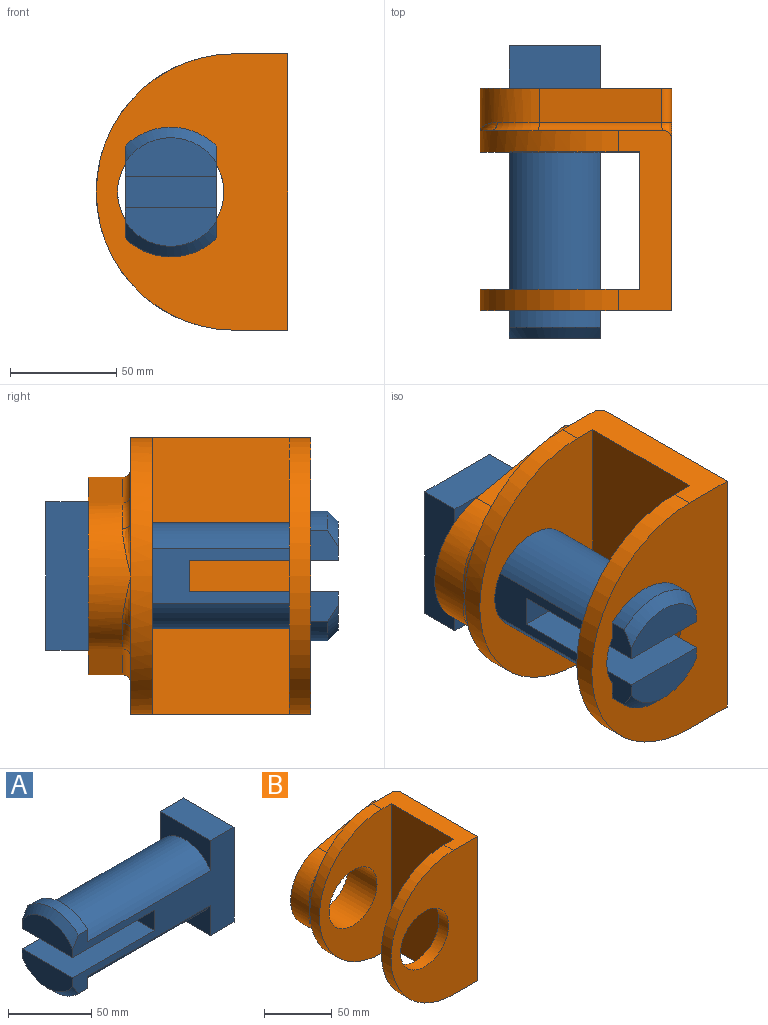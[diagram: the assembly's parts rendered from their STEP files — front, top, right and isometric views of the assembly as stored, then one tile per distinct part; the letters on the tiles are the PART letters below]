
ASSEMBLY  parts=2 mates=1
PART A: 20 faces, bbox 137.5x51.4x70 mm
  f0: plane 43x18mm, normal (-1,0,0), area 624.6mm2, adj f1,f7,f11,f19
  f1: plane 137.5x70mm, normal (0,-1,0), area 3540.9mm2, adj f0,f2,f3,f4,f5,f6,f8,f9
  f2: plane 43x22.24mm, normal (-1,0,0), area 583.7mm2, adj f1,f4,f7,f16
  f3: plane 70x43mm, normal (1,0,0), area 3010mm2, adj f1,f4,f6,f7
  f4: plane 43x20mm, normal (0,0,1), area 860mm2, adj f1,f2,f3,f7
  f5: plane 43x22.24mm, normal (-1,0,0), area 583.7mm2, adj f1,f6,f7,f15
  f6: plane 43x20mm, normal (0,0,-1), area 860mm2, adj f1,f3,f5,f7
  f7: plane 137.5x70mm, normal (0,1,0), area 3540.9mm2, adj f0,f2,f3,f4,f5,f6,f8,f9
  f8: cylinder r=30.5mm len=43mm, axis (1,0,0), area 381.8mm2, adj f1,f7,f14,f18
  f9: cylinder r=30.5mm len=43mm, axis (1,0,0), area 381.8mm2, adj f1,f7,f17,f19
  f10: plane 43x18mm, normal (-1,0,0), area 624.6mm2, adj f1,f7,f12,f18
  f11: plane 70x43mm, normal (0,0,-1), area 3010mm2, adj f0,f1,f7,f13
  f12: plane 70x43mm, normal (0,0,1), area 3010mm2, adj f1,f7,f10,f13
  f13: plane 43x15mm, normal (-1,0,0), area 645mm2, adj f1,f7,f11,f12
  f14: plane 43x17.74mm, normal (1,0,0), area 271.5mm2, adj f1,f7,f8,f15
  f15: cylinder r=25mm len=104.5mm, axis (1,0,0), area 5409.3mm2, adj f1,f5,f7,f14
  f16: cylinder r=25mm len=104.5mm, axis (1,0,0), area 5409.3mm2, adj f1,f2,f7,f17
  f17: plane 43x17.74mm, normal (1,0,0), area 271.5mm2, adj f1,f7,f9,f16
  f18: cone r=25.5mm half-angle=45deg, axis (1,0,0), area 347.6mm2, adj f1,f7,f8,f10
  f19: cone r=25.5mm half-angle=45deg, axis (1,0,0), area 347.6mm2, adj f0,f1,f7,f9
PART B: 29 faces, bbox 90x104.5x130 mm
  f0: plane 81.07x40.16mm, normal (0,1,0), area 1246.8mm2, adj f4,f5,f18,f19,f22
  f1: cylinder r=65mm len=130mm, axis (0,1,0), area 2042mm2, adj f2,f4,f6,f9
  f2: plane 84.5x25mm, normal (0,0,-1), area 1464.1mm2, adj f1,f3,f5,f6,f7,f8,f9,f10
  f3: plane 130x104.5mm, normal (1,0,0), area 12533.2mm2, adj f2,f4,f6,f14,f20,f21,f22,f26
  f4: plane 84.5x25mm, normal (0,0,1), area 1464.1mm2, adj f0,f1,f3,f5,f6,f8,f9,f10
  f5: cylinder r=65mm len=130mm, axis (0,1,0), area 2042mm2, adj f0,f2,f4,f7,f8,f17,f23
  f6: plane 130x90mm, normal (0,-1,0), area 7923.1mm2, adj f1,f2,f3,f4,f16
  f7: plane 81.07x40.16mm, normal (0,1,0), area 1246.8mm2, adj f2,f5,f24,f25,f26
  f8: plane 130x75mm, normal (0,-1,0), area 5973.1mm2, adj f2,f4,f5,f10,f15
  f9: plane 130x75mm, normal (0,1,0), area 5973.1mm2, adj f1,f2,f4,f10,f16
  f10: plane 130x64.5mm, normal (-1,0,0), area 8385mm2, adj f2,f4,f8,f9
  f11: cylinder r=35mm len=68.48mm, axis (0,-1,0), area 1600.5mm2, adj f12,f13,f14,f17,f18,f23,f24
  f12: plane 57.43x16mm, normal (-0.21,0,0.98), area 939.3mm2, adj f11,f14,f19,f20
  f13: plane 57.43x16mm, normal (-0.21,0,-0.98), area 939.3mm2, adj f11,f14,f25,f28
  f14: plane 93.01x90mm, normal (0,1,0), area 4530.5mm2, adj f3,f11,f12,f13,f15,f20,f28
  f15: cylinder r=25mm len=50mm, axis (0,1,0), area 4712.4mm2, adj f8,f14
  f16: cylinder r=25mm len=50mm, axis (0,1,0), area 1570.8mm2, adj f6,f9
  f17: bspline ~27.41x9.77mm, area 73.2mm2, adj f5,f11,f18
  f18: torus R=39mm, axis (0,-1,0), area 153.8mm2, adj f0,f11,f17,f19
  f19: cylinder r=4mm len=59.92mm, axis (-0.98,0,-0.21), area 372.7mm2, adj f0,f12,f18,f21
  f20: cylinder r=4mm len=16mm, axis (0,-1,0), area 113.9mm2, adj f3,f12,f14,f21
  f21: bspline ~8.53x8mm, area 58.1mm2, adj f3,f19,f20,f22
  f22: cylinder r=4mm len=14.32mm, axis (0,0,1), area 90mm2, adj f0,f3,f4,f21
  f23: bspline ~27.41x9.77mm, area 73.2mm2, adj f5,f11,f24
  f24: torus R=39mm, axis (0,-1,0), area 153.8mm2, adj f7,f11,f23,f25
  f25: cylinder r=4mm len=59.92mm, axis (0.98,0,-0.21), area 372.7mm2, adj f7,f13,f24,f27
  f26: cylinder r=4mm len=14.32mm, axis (0,0,1), area 90mm2, adj f2,f3,f7,f27
  f27: bspline ~9.6x8.35mm, area 58.1mm2, adj f3,f25,f26,f28
  f28: cylinder r=4mm len=16mm, axis (0,1,0), area 113.9mm2, adj f3,f13,f14,f27
PLACE A rot(axis=(0,0,1),90deg) t=(-79.23,-31.5,-20.98)mm
PLACE B t=(-79.23,-63.95,-20.98)mm
MATE revolute A.f15 <-> B.f15  axis (0,1,0) through (-79.23,-106.2,-20.98)mm
